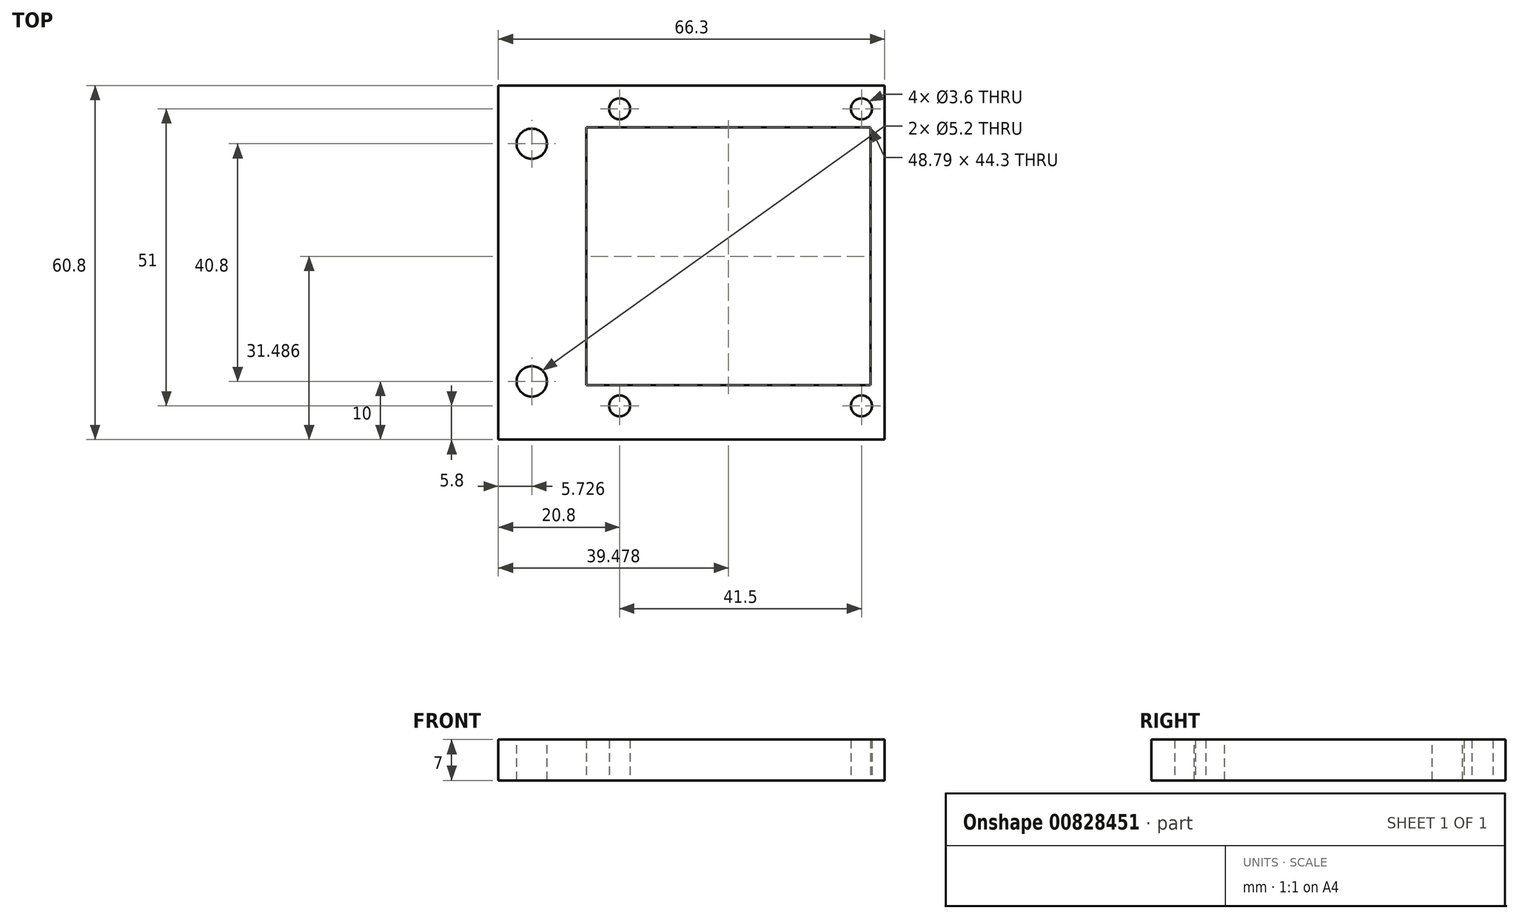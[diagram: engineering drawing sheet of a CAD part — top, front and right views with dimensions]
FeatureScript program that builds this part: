
annotation { "Feature Type Name" : "Feature", "Feature Type Description" : "" }
export const myFeature = defineFeature(function(context is Context, id is Id, definition is map)
    precondition{}
    {
        {
            var Q0;
            Q0=qCreatedBy(makeId("Top.planeOp"),FACE);
            var sketch = newSketch(context, id + "F0", { "sketchPlane" : qUnion([Q0])});
            skLineSegment(sketch, "E0.bottom", {"start": v(0, 0) * mm, "end": v(51.3, 0) * mm});
            skLineSegment(sketch, "E0.top", {"start": v(0, -60.8) * mm, "end": v(51.3, -60.8) * mm});
            skLineSegment(sketch, "E0.left", {"start": v(0, 0) * mm, "end": v(0, -60.8) * mm});
            skLineSegment(sketch, "E0.right", {"start": v(51.3, 0) * mm, "end": v(51.3, -60.8) * mm});
            skCircle(sketch, "E1", {"center": v(5.8, -4) * mm, "radius": 1.8 * mm});
            skCircle(sketch, "E2", {"center": v(5.8, -55) * mm, "radius": 1.8 * mm});
            skCircle(sketch, "E3", {"center": v(47.3, -55) * mm, "radius": 1.8 * mm});
            skCircle(sketch, "E4", {"center": v(47.3, -4) * mm, "radius": 1.8 * mm});
            skLineSegment(sketch, "E5", {"start": v(5.8, -56.8) * mm, "end": v(5.8, -60.8) * mm, "construction": true});
            skLineSegment(sketch, "E6", {"start": v(4, -55) * mm, "end": v(0, -55) * mm, "construction": true});
            skLineSegment(sketch, "E7", {"start": v(47.3, -4) * mm, "end": v(51.3, -4) * mm, "construction": true});
            skLineSegment(sketch, "E8", {"start": v(47.3, -4) * mm, "end": v(47.3, 0) * mm, "construction": true});
            skLineSegment(sketch, "E9.bottom", {"start": v(0.08, -7.16) * mm, "end": v(48.87, -7.16) * mm});
            skLineSegment(sketch, "E9.top", {"start": v(0.08, -51.46) * mm, "end": v(48.87, -51.46) * mm});
            skLineSegment(sketch, "E9.left", {"start": v(0.08, -7.16) * mm, "end": v(0.08, -51.46) * mm});
            skLineSegment(sketch, "E9.right", {"start": v(48.87, -7.16) * mm, "end": v(48.87, -51.46) * mm});
            skSolve(sketch);
        }
        {
            var Q0;
            Q0=makeQuery(id+"F0.imprint","IMPRINT",FACE,{"disambiguationData":[TD([[makeQuery(id+"F0.imprint","IMPRINT",EDGE,{"derivedFrom":sQuery(id+"F0.wireOp",EDGE,"E0.bottom")}),-1.0]])]});
            extrude(context, id + "F1", {"entities" : qUnion([Q0]), "depth" : 7 * mm, "offsetDistance" : 25 * mm});
        }
        {
            var Q0;
            Q0=makeQuery(id+"F1.opExtrude","SWEPT_FACE",FACE,{"disambiguationData":[OSD([sQuery(id+"F0.wireOp",EDGE,"E0.left")])]});
            extrude(context, id + "F2", {"entities" : qUnion([Q0]), "operationType" : NewBodyOperationType.ADD, "depth" : 15 * mm, "offsetDistance" : 25 * mm});
        }
        {
            var Q0;
            {var subQ0=sQuery(id+"F0.wireOp",EDGE,"E0.left");Q0=makeQuery(id+"F2.boolean.opBoolean","MERGE",FACE,{"derivedFrom":[makeQuery(id+"F1.opExtrude","CAP_FACE",FACE,{"disambiguationData":[OSD([sQuery(id+"F0.wireOp",EDGE,"E0.bottom"),sQuery(id+"F0.wireOp",EDGE,"E0.top"),subQ0,sQuery(id+"F0.wireOp",EDGE,"E0.right"),sQuery(id+"F0.wireOp",EDGE,"R8pAmf2F-biWS-PgLo-OTuY-xoEfuvJFqgsZ.bottom"),sQuery(id+"F0.wireOp",EDGE,"R8pAmf2F-biWS-PgLo-OTuY-xoEfuvJFqgsZ.top"),sQuery(id+"F0.wireOp",EDGE,"R8pAmf2F-biWS-PgLo-OTuY-xoEfuvJFqgsZ.left"),sQuery(id+"F0.wireOp",EDGE,"R8pAmf2F-biWS-PgLo-OTuY-xoEfuvJFqgsZ.right"),sQuery(id+"F0.wireOp",EDGE,"E1"),sQuery(id+"F0.wireOp",EDGE,"E2"),sQuery(id+"F0.wireOp",EDGE,"E3"),sQuery(id+"F0.wireOp",EDGE,"E4")])],"isStart":false}),makeQuery(id+"F2.opExtrude","SWEPT_FACE",FACE,{"disambiguationData":[OSD([subQ0]),TDD([makeQuery(id+"F1.opExtrude","CAP_EDGE",EDGE,{"disambiguationData":[OSD([subQ0])],"isStart":false})])]})]});}
            var sketch = newSketch(context, id + "F3", { "sketchPlane" : qUnion([Q0])});
            skCircle(sketch, "E10", {"center": v(-9.27, -10) * mm, "radius": 2.6 * mm});
            skCircle(sketch, "E11", {"center": v(-9.27, -50.8) * mm, "radius": 2.6 * mm});
            skLineSegment(sketch, "E12", {"start": v(-9.27, -10) * mm, "end": v(-9.27, -50.8) * mm, "construction": true});
            skLineSegment(sketch, "E13", {"start": v(-9.27, -10) * mm, "end": v(-9.27, 0) * mm, "construction": true});
            skLineSegment(sketch, "E14", {"start": v(-9.27, -50.8) * mm, "end": v(-9.27, -60.8) * mm, "construction": true});
            skSolve(sketch);
        }
        {
            var Q0;
            Q0=makeQuery(id+"F3.imprint","IMPRINT",FACE,{"disambiguationData":[TD([[makeQuery(id+"F3.imprint","IMPRINT",EDGE,{"derivedFrom":sQuery(id+"F3.wireOp",EDGE,"E10")}),1.0]])]});
            var Q1;
            Q1=makeQuery(id+"F3.imprint","IMPRINT",FACE,{"disambiguationData":[TD([[makeQuery(id+"F3.imprint","IMPRINT",EDGE,{"derivedFrom":sQuery(id+"F3.wireOp",EDGE,"E11")}),1.0]])]});
            extrude(context, id + "F4", {"entities" : qUnion([Q0, Q1]), "operationType" : NewBodyOperationType.REMOVE, "oppositeDirection" : true, "depth" : 25 * mm, "offsetDistance" : 25 * mm});
        }
    });
